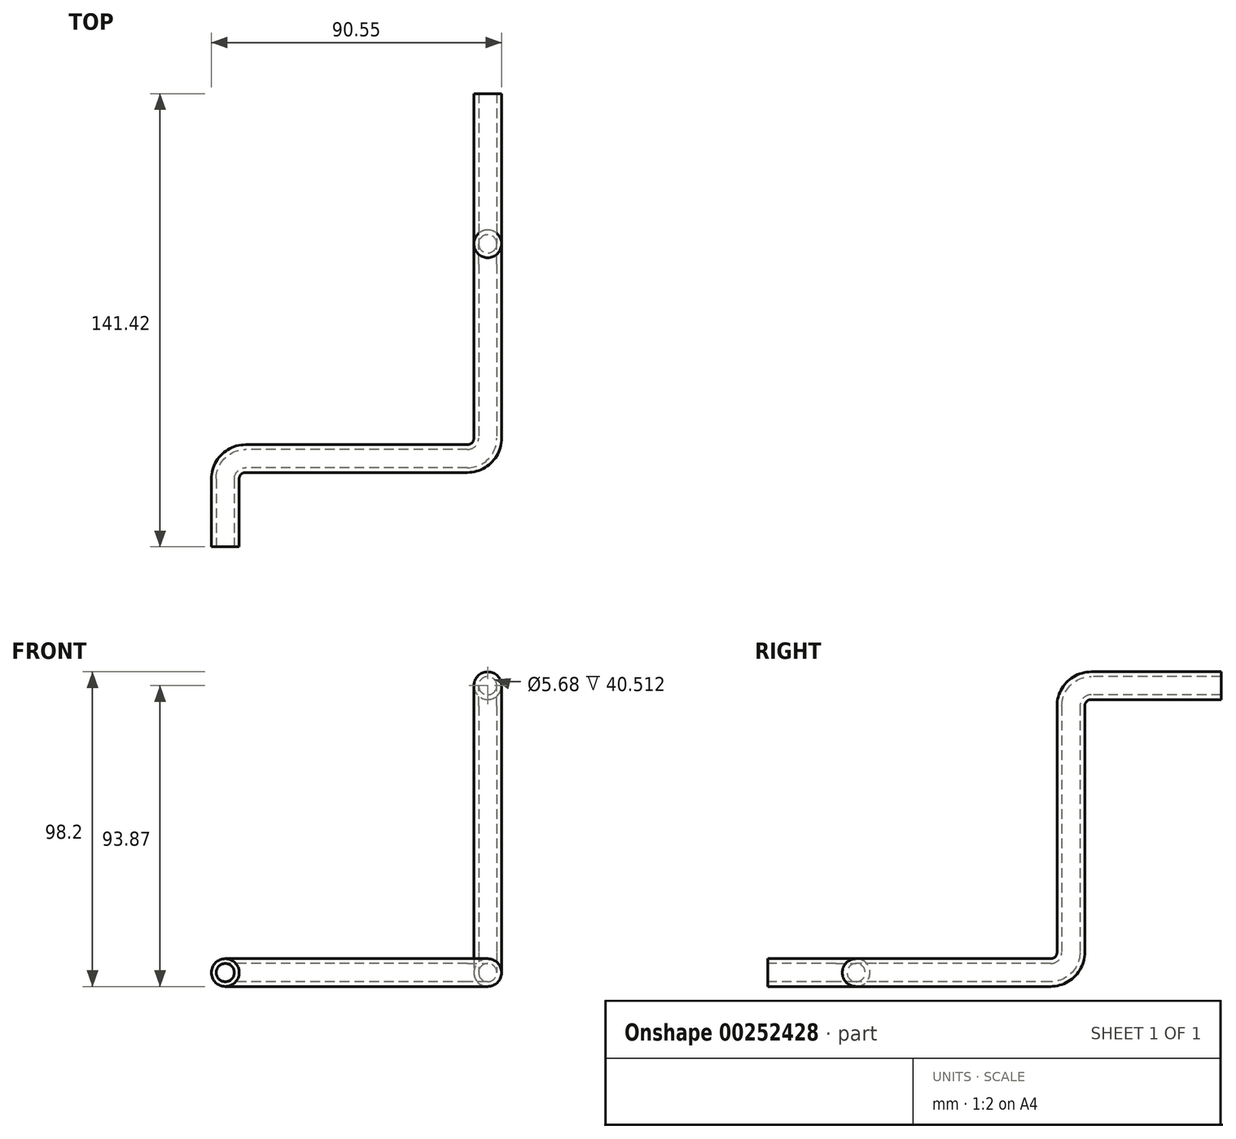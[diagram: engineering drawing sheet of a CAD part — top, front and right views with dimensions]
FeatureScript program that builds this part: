
annotation { "Feature Type Name" : "Feature", "Feature Type Description" : "" }
export const myFeature = defineFeature(function(context is Context, id is Id, definition is map)
    precondition{}
    {
        {
            var Q0;
            Q0=qCreatedBy(makeId("Front.planeOp"),FACE);
            var sketch = newSketch(context, id + "F0", { "sketchPlane" : qUnion([Q0])});
            skCircle(sketch, "E0", {"center": v(0, 0) * mm, "radius": 4.33 * mm});
            skCircle(sketch, "E1", {"center": v(0, 0) * mm, "radius": 2.84 * mm});
            skSolve(sketch);
        }
        {
            var Q0;
            Q0=qCreatedBy(makeId("Right.planeOp"),FACE);
            var sketch = newSketch(context, id + "F1", { "sketchPlane" : qUnion([Q0])});
            skLineSegment(sketch, "E2", {"start": v(0, 0) * mm, "end": v(-40.51, 0) * mm});
            skLineSegment(sketch, "E3", {"start": v(-46.86, -6.35) * mm, "end": v(-46.86, -83.19) * mm});
            skLineSegment(sketch, "E4", {"start": v(-53.21, -89.54) * mm, "end": v(-93.2, -89.54) * mm});
            skPoint(sketch, "E5.visualSharp", {"position": v(-46.86, 0) * mm});
            skArc(sketch, "E5.filletArc", {"start": v(-40.51, 0) * mm, "mid": v(-45, -1.86) * mm, "end": v(-46.86, -6.35) * mm});
            skPoint(sketch, "E6.visualSharp", {"position": v(-46.86, -89.54) * mm});
            skArc(sketch, "E6.filletArc", {"start": v(-53.21, -89.54) * mm, "mid": v(-48.72, -87.68) * mm, "end": v(-46.86, -83.19) * mm});
            skSolve(sketch);
        }
        {
            var Q0;
            Q0=makeQuery(id+"F0.imprint","IMPRINT",FACE,{"disambiguationData":[TD([[makeQuery(id+"F0.imprint","IMPRINT",EDGE,{"derivedFrom":sQuery(id+"F0.wireOp",EDGE,"E0")}),1.0]])]});
            var Q1;
            Q1=sQuery(id+"F1.wireOp",EDGE,"E4");
            var Q2;
            Q2=sQuery(id+"F1.wireOp",EDGE,"E5.filletArc");
            var Q3;
            Q3=sQuery(id+"F1.wireOp",EDGE,"E2");
            var Q4;
            Q4=sQuery(id+"F1.wireOp",EDGE,"E3");
            var Q5;
            Q5=sQuery(id+"F1.wireOp",EDGE,"E6.filletArc");
            sweep(context, id + "F2", {"profiles" : qUnion([Q0]), "path" : qUnion([Q1, Q2, Q3, Q4, Q5])});
        }
        {
            var Q0;
            Q0=makeQuery(id+"F2.opSweep","CAP_FACE",FACE,{"disambiguationData":[OSD([sQuery(id+"F0.wireOp",EDGE,"E0"),sQuery(id+"F0.wireOp",EDGE,"E1"),sQuery(id+"F1.wireOp",VERTEX,"E4.end")])],"isStart":false});
            var sketch = newSketch(context, id + "F3", { "sketchPlane" : qUnion([Q0])});
            skCircle(sketch, "E7.0", {"center": v(0, -89.54) * mm, "radius": 2.84 * mm});
            skSolve(sketch);
        }
        {
            var Q0;
            Q0=sQuery(id+"F3.wireOp",VERTEX,"E7.0.center");
            var Q1;
            Q1=qCreatedBy(makeId("Top.planeOp"),FACE);
            cPlane(context, id + "F4", {"entities" : qUnion([Q0, Q1]), "cplaneType" : CPlaneType.PLANE_POINT, "offset" : 25.4 * mm, "width" : 152.4 * mm, "height" : 152.4 * mm});
        }
        {
            var Q0;
            Q0=qCreatedBy(id+"F4.planeOp",FACE);
            var sketch = newSketch(context, id + "F5", { "sketchPlane" : qUnion([Q0])});
            skLineSegment(sketch, "E8", {"start": v(0, -93.2) * mm, "end": v(0, -107.53) * mm});
            skLineSegment(sketch, "E9", {"start": v(-6.35, -113.88) * mm, "end": v(-75.54, -113.88) * mm});
            skLineSegment(sketch, "E10", {"start": v(-81.9, -120.23) * mm, "end": v(-81.9, -141.42) * mm});
            skPoint(sketch, "E11.visualSharp", {"position": v(0, -113.88) * mm});
            skArc(sketch, "E11.filletArc", {"start": v(-6.35, -113.88) * mm, "mid": v(-1.86, -112.02) * mm, "end": v(0, -107.53) * mm});
            skPoint(sketch, "E12.visualSharp", {"position": v(-81.9, -113.88) * mm});
            skArc(sketch, "E12.filletArc", {"start": v(-75.54, -113.88) * mm, "mid": v(-80.03, -115.74) * mm, "end": v(-81.9, -120.23) * mm});
            skSolve(sketch);
        }
        {
            var Q0;
            Q0=makeQuery(id+"F3.imprint","IMPRINT",FACE,{"disambiguationData":[TD([[makeQuery(id+"F3.imprint","IMPRINT",EDGE,{"derivedFrom":sQuery(id+"F3.wireOp",EDGE,"E7.0")}),-1.0]])]});
            var Q1;
            Q1=sQuery(id+"F5.wireOp",EDGE,"E10");
            var Q2;
            Q2=sQuery(id+"F5.wireOp",EDGE,"E12.filletArc");
            var Q3;
            Q3=sQuery(id+"F5.wireOp",EDGE,"E9");
            var Q4;
            Q4=sQuery(id+"F5.wireOp",EDGE,"E11.filletArc");
            var Q5;
            Q5=sQuery(id+"F5.wireOp",EDGE,"E8");
            sweep(context, id + "F6", {"operationType" : NewBodyOperationType.ADD, "profiles" : qUnion([Q0]), "path" : qUnion([Q1, Q2, Q3, Q4, Q5])});
        }
    });
